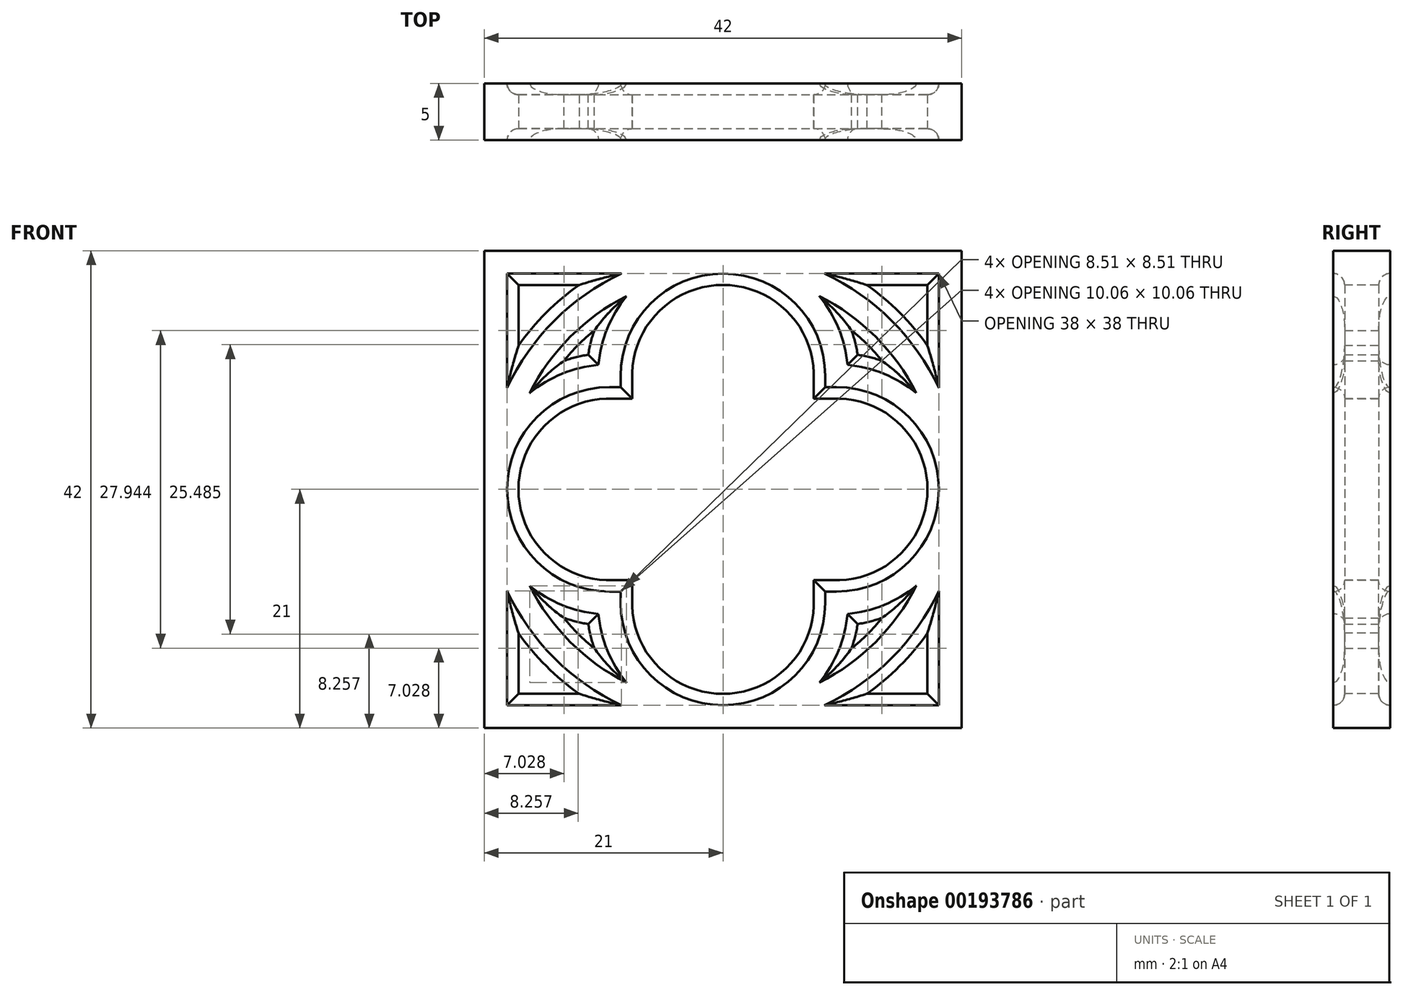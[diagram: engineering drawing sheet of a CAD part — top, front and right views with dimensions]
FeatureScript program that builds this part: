
annotation { "Feature Type Name" : "Feature", "Feature Type Description" : "" }
export const myFeature = defineFeature(function(context is Context, id is Id, definition is map)
    precondition{}
    {
        {
            var Q0;
            Q0=qCreatedBy(makeId("Right.planeOp"),FACE);
            var sketch = newSketch(context, id + "F0", { "sketchPlane" : qUnion([Q0])});
            skLineSegment(sketch, "E0", {"start": v(0, 0) * mm, "end": v(0, 20) * mm, "construction": true});
            skLineSegment(sketch, "E1.bottom", {"start": v(2.5, 21) * mm, "end": v(-2.5, 21) * mm});
            skLineSegment(sketch, "E1.top", {"start": v(2.5, 19) * mm, "end": v(-2.5, 19) * mm});
            skLineSegment(sketch, "E1.left", {"start": v(2.5, 21) * mm, "end": v(2.5, 19) * mm});
            skLineSegment(sketch, "E1.right", {"start": v(-2.5, 21) * mm, "end": v(-2.5, 19) * mm});
            skPoint(sketch, "E1.middle", {"position": v(0, 20) * mm});
            skLineSegment(sketch, "E2.bottom", {"start": v(-1.5, 22) * mm, "end": v(1.5, 22) * mm});
            skLineSegment(sketch, "E2.top", {"start": v(-1.5, 18) * mm, "end": v(1.5, 18) * mm});
            skLineSegment(sketch, "E2.left", {"start": v(-1.5, 22) * mm, "end": v(-1.5, 18) * mm});
            skLineSegment(sketch, "E2.right", {"start": v(1.5, 22) * mm, "end": v(1.5, 18) * mm});
            skArc(sketch, "E3", {"start": v(-2.5, 21) * mm, "mid": v(-1.8, 21.3) * mm, "end": v(-1.5, 22) * mm});
            skArc(sketch, "E4", {"start": v(-1.5, 18) * mm, "mid": v(-1.8, 18.7) * mm, "end": v(-2.5, 19) * mm});
            skArc(sketch, "E5", {"start": v(1.5, 22) * mm, "mid": v(1.8, 21.3) * mm, "end": v(2.5, 21) * mm});
            skArc(sketch, "E6", {"start": v(2.5, 19) * mm, "mid": v(1.8, 18.7) * mm, "end": v(1.5, 18) * mm});
            skLineSegment(sketch, "E7", {"start": v(0, 0) * mm, "end": v(-9.88, 0) * mm, "construction": true});
            skLineSegment(sketch, "E8", {"start": v(-2.5, 20) * mm, "end": v(2.5, 20) * mm});
            skSolve(sketch);
        }
        {
            var Q0;
            Q0=qCreatedBy(makeId("Front.planeOp"),FACE);
            var sketch = newSketch(context, id + "F1", { "sketchPlane" : qUnion([Q0])});
            skCircle(sketch, "E9", {"center": v(0, 0) * mm, "radius": 20 * mm});
            skLineSegment(sketch, "E10", {"start": v(0, 0) * mm, "end": v(20, 0) * mm, "construction": true});
            skLineSegment(sketch, "E11", {"start": v(0, 0) * mm, "end": v(-20, 0) * mm, "construction": true});
            skLineSegment(sketch, "E12", {"start": v(0, 0) * mm, "end": v(0, -20) * mm, "construction": true});
            skLineSegment(sketch, "E13", {"start": v(0, -20) * mm, "end": v(20, -20) * mm});
            skLineSegment(sketch, "E14", {"start": v(20, -20) * mm, "end": v(20, 0) * mm});
            skLineSegment(sketch, "E15", {"start": v(0, 0) * mm, "end": v(0, 20) * mm, "construction": true});
            skLineSegment(sketch, "E16", {"start": v(0, 20) * mm, "end": v(20, 20) * mm});
            skLineSegment(sketch, "E17", {"start": v(20, 20) * mm, "end": v(20, 0) * mm});
            skLineSegment(sketch, "E18", {"start": v(0, 20) * mm, "end": v(-20, 20) * mm});
            skLineSegment(sketch, "E19", {"start": v(-20, 20) * mm, "end": v(-20, 0) * mm});
            skLineSegment(sketch, "E20", {"start": v(0, -20) * mm, "end": v(-20, -20) * mm});
            skLineSegment(sketch, "E21", {"start": v(-20, -20) * mm, "end": v(-20, 0) * mm});
            skCircle(sketch, "E22", {"center": v(-10, 0) * mm, "radius": 10 * mm, "construction": true});
            skCircle(sketch, "E23", {"center": v(0, 10) * mm, "radius": 10 * mm, "construction": true});
            skCircle(sketch, "E24", {"center": v(10, 0) * mm, "radius": 10 * mm, "construction": true});
            skCircle(sketch, "E25", {"center": v(0, -10) * mm, "radius": 10 * mm, "construction": true});
            skArc(sketch, "E26", {"start": v(0, 20) * mm, "mid": v(-7.07, 17.07) * mm, "end": v(-10, 10) * mm});
            skArc(sketch, "E27", {"start": v(-10, 10) * mm, "mid": v(-17.07, 7.07) * mm, "end": v(-20, 0) * mm});
            skArc(sketch, "E28", {"start": v(-20, 0) * mm, "mid": v(-17.07, -7.07) * mm, "end": v(-10, -10) * mm});
            skArc(sketch, "E29", {"start": v(0, 20) * mm, "mid": v(7.07, 17.07) * mm, "end": v(10, 10) * mm});
            skArc(sketch, "E30", {"start": v(10, 10) * mm, "mid": v(17.07, 7.07) * mm, "end": v(20, 0) * mm});
            skArc(sketch, "E31", {"start": v(20, 0) * mm, "mid": v(17.07, -7.07) * mm, "end": v(10, -10) * mm});
            skArc(sketch, "E32", {"start": v(0, -20) * mm, "mid": v(7.07, -17.07) * mm, "end": v(10, -10) * mm});
            skArc(sketch, "E33", {"start": v(0, -20) * mm, "mid": v(-7.07, -17.07) * mm, "end": v(-10, -10) * mm});
            skLineSegment(sketch, "E34", {"start": v(0, 20) * mm, "end": v(0, 25) * mm, "construction": true});
            skLineSegment(sketch, "E35", {"start": v(0, 25) * mm, "end": v(25, 25) * mm});
            skLineSegment(sketch, "E36", {"start": v(25, 25) * mm, "end": v(25, -25) * mm});
            skLineSegment(sketch, "E37", {"start": v(25, -25) * mm, "end": v(-25, -25) * mm});
            skLineSegment(sketch, "E38", {"start": v(-25, -25) * mm, "end": v(-25, 25) * mm});
            skLineSegment(sketch, "E39", {"start": v(-25, 25) * mm, "end": v(0, 25) * mm});
            skPoint(sketch, "E40.0", {"position": v(0, 21) * mm});
            skLineSegment(sketch, "E41", {"start": v(0, 21) * mm, "end": v(21, 21) * mm});
            skLineSegment(sketch, "E42", {"start": v(21, 21) * mm, "end": v(21, -21) * mm});
            skLineSegment(sketch, "E43", {"start": v(21, -21) * mm, "end": v(-21, -21) * mm});
            skLineSegment(sketch, "E44", {"start": v(-21, -21) * mm, "end": v(-21, 21) * mm});
            skLineSegment(sketch, "E45", {"start": v(-21, 21) * mm, "end": v(0, 21) * mm});
            skSolve(sketch);
        }
        {
            var Q0;
            {var subQ0=sQuery(id+"F0.wireOp",EDGE,"E5");Q0=makeQuery(id+"F0.imprint","IMPRINT",FACE,{"disambiguationData":[TD([[makeQuery(id+"F0.imprint","IMPRINT",EDGE,{"derivedFrom":subQ0}),-1.0]])]});}
            var Q1;
            {var subQ1=sQuery(id+"F0.wireOp",EDGE,"E1.bottom");var subQ3=sQuery(id+"F0.wireOp",EDGE,"E2.right");var subQ4=makeQuery(id+"F0.imprint","INTERSECT",VERTEX,{"derivedFrom":[subQ1,subQ3]});Q1=makeQuery(id+"F0.imprint","IMPRINT",FACE,{"disambiguationData":[TD([[makeQuery(id+"F0.imprint","IMPRINT",EDGE,{"disambiguationData":[TD([[subQ4,-1.0]])],"derivedFrom":subQ3}),1.0]])]});}
            var Q2;
            {var subQ0=sQuery(id+"F0.wireOp",EDGE,"E2.right");var subQ1=sQuery(id+"F0.wireOp",EDGE,"E1.bottom");var subQ2=makeQuery(id+"F0.imprint","INTERSECT",VERTEX,{"derivedFrom":[subQ1,subQ0]});Q2=makeQuery(id+"F0.imprint","IMPRINT",FACE,{"disambiguationData":[TD([[makeQuery(id+"F0.imprint","IMPRINT",EDGE,{"disambiguationData":[TD([[subQ2,-1.0]])],"derivedFrom":subQ1}),1.0]])]});}
            var Q3;
            {var subQ5=sQuery(id+"F0.wireOp",EDGE,"E2.bottom");Q3=makeQuery(id+"F0.imprint","IMPRINT",FACE,{"disambiguationData":[TD([[makeQuery(id+"F0.imprint","IMPRINT",EDGE,{"derivedFrom":subQ5}),-1.0]])]});}
            var Q4;
            {var subQ0=sQuery(id+"F0.wireOp",EDGE,"E3");Q4=makeQuery(id+"F0.imprint","IMPRINT",FACE,{"disambiguationData":[TD([[makeQuery(id+"F0.imprint","IMPRINT",EDGE,{"derivedFrom":subQ0}),-1.0]])]});}
            var Q5;
            {var subQ1=sQuery(id+"F0.wireOp",EDGE,"E1.bottom");var subQ3=sQuery(id+"F0.wireOp",EDGE,"E2.left");var subQ4=makeQuery(id+"F0.imprint","INTERSECT",VERTEX,{"derivedFrom":[subQ1,subQ3]});Q5=makeQuery(id+"F0.imprint","IMPRINT",FACE,{"disambiguationData":[TD([[makeQuery(id+"F0.imprint","IMPRINT",EDGE,{"disambiguationData":[TD([[subQ4,-1.0]])],"derivedFrom":subQ3}),-1.0]])]});}
            var Q6;
            {var subQ1=sQuery(id+"F0.wireOp",EDGE,"E1.top");var subQ3=sQuery(id+"F0.wireOp",EDGE,"E2.left");var subQ4=makeQuery(id+"F0.imprint","INTERSECT",VERTEX,{"derivedFrom":[subQ1,subQ3]});Q6=makeQuery(id+"F0.imprint","IMPRINT",FACE,{"disambiguationData":[TD([[makeQuery(id+"F0.imprint","IMPRINT",EDGE,{"disambiguationData":[TD([[subQ4,1.0]])],"derivedFrom":subQ3}),-1.0]])]});}
            var Q7;
            {var subQ0=sQuery(id+"F0.wireOp",EDGE,"E2.right");var subQ1=sQuery(id+"F0.wireOp",EDGE,"E1.top");var subQ2=makeQuery(id+"F0.imprint","INTERSECT",VERTEX,{"derivedFrom":[subQ1,subQ0]});Q7=makeQuery(id+"F0.imprint","IMPRINT",FACE,{"disambiguationData":[TD([[makeQuery(id+"F0.imprint","IMPRINT",EDGE,{"disambiguationData":[TD([[subQ2,-1.0]])],"derivedFrom":subQ1}),-1.0]])]});}
            var Q8;
            {var subQ5=sQuery(id+"F0.wireOp",EDGE,"E2.top");Q8=makeQuery(id+"F0.imprint","IMPRINT",FACE,{"disambiguationData":[TD([[makeQuery(id+"F0.imprint","IMPRINT",EDGE,{"derivedFrom":subQ5}),1.0]])]});}
            var Q9;
            {var subQ0=sQuery(id+"F0.wireOp",EDGE,"E4");Q9=makeQuery(id+"F0.imprint","IMPRINT",FACE,{"disambiguationData":[TD([[makeQuery(id+"F0.imprint","IMPRINT",EDGE,{"derivedFrom":subQ0}),-1.0]])]});}
            var Q10;
            {var subQ1=sQuery(id+"F0.wireOp",EDGE,"E1.top");var subQ3=sQuery(id+"F0.wireOp",EDGE,"E2.right");var subQ4=makeQuery(id+"F0.imprint","INTERSECT",VERTEX,{"derivedFrom":[subQ1,subQ3]});Q10=makeQuery(id+"F0.imprint","IMPRINT",FACE,{"disambiguationData":[TD([[makeQuery(id+"F0.imprint","IMPRINT",EDGE,{"disambiguationData":[TD([[subQ4,1.0]])],"derivedFrom":subQ3}),1.0]])]});}
            var Q11;
            {var subQ0=sQuery(id+"F0.wireOp",EDGE,"E6");Q11=makeQuery(id+"F0.imprint","IMPRINT",FACE,{"disambiguationData":[TD([[makeQuery(id+"F0.imprint","IMPRINT",EDGE,{"derivedFrom":subQ0}),-1.0]])]});}
            var Q12;
            Q12=sQuery(id+"F1.wireOp",EDGE,"E9");
            sweep(context, id + "F2", {"profiles" : qUnion([Q0, Q1, Q2, Q3, Q4, Q5, Q6, Q7, Q8, Q9, Q10, Q11]), "path" : qUnion([Q12])});
        }
        {
            var Q0;
            {var subQ1=sQuery(id+"F0.wireOp",EDGE,"E1.bottom");var subQ3=sQuery(id+"F0.wireOp",EDGE,"E2.left");var subQ4=makeQuery(id+"F0.imprint","INTERSECT",VERTEX,{"derivedFrom":[subQ1,subQ3]});Q0=makeQuery(id+"F0.imprint","IMPRINT",FACE,{"disambiguationData":[TD([[makeQuery(id+"F0.imprint","IMPRINT",EDGE,{"disambiguationData":[TD([[subQ4,-1.0]])],"derivedFrom":subQ3}),-1.0]])]});}
            var Q1;
            {var subQ1=sQuery(id+"F0.wireOp",EDGE,"E1.top");var subQ3=sQuery(id+"F0.wireOp",EDGE,"E2.left");var subQ4=makeQuery(id+"F0.imprint","INTERSECT",VERTEX,{"derivedFrom":[subQ1,subQ3]});Q1=makeQuery(id+"F0.imprint","IMPRINT",FACE,{"disambiguationData":[TD([[makeQuery(id+"F0.imprint","IMPRINT",EDGE,{"disambiguationData":[TD([[subQ4,1.0]])],"derivedFrom":subQ3}),-1.0]])]});}
            var Q2;
            {var subQ0=sQuery(id+"F0.wireOp",EDGE,"E2.right");var subQ1=sQuery(id+"F0.wireOp",EDGE,"E1.bottom");var subQ2=makeQuery(id+"F0.imprint","INTERSECT",VERTEX,{"derivedFrom":[subQ1,subQ0]});Q2=makeQuery(id+"F0.imprint","IMPRINT",FACE,{"disambiguationData":[TD([[makeQuery(id+"F0.imprint","IMPRINT",EDGE,{"disambiguationData":[TD([[subQ2,-1.0]])],"derivedFrom":subQ1}),1.0]])]});}
            var Q3;
            {var subQ0=sQuery(id+"F0.wireOp",EDGE,"E2.right");var subQ1=sQuery(id+"F0.wireOp",EDGE,"E1.top");var subQ2=makeQuery(id+"F0.imprint","INTERSECT",VERTEX,{"derivedFrom":[subQ1,subQ0]});Q3=makeQuery(id+"F0.imprint","IMPRINT",FACE,{"disambiguationData":[TD([[makeQuery(id+"F0.imprint","IMPRINT",EDGE,{"disambiguationData":[TD([[subQ2,-1.0]])],"derivedFrom":subQ1}),-1.0]])]});}
            var Q4;
            {var subQ0=sQuery(id+"F0.wireOp",EDGE,"E4");Q4=makeQuery(id+"F0.imprint","IMPRINT",FACE,{"disambiguationData":[TD([[makeQuery(id+"F0.imprint","IMPRINT",EDGE,{"derivedFrom":subQ0}),-1.0]])]});}
            var Q5;
            {var subQ5=sQuery(id+"F0.wireOp",EDGE,"E2.top");Q5=makeQuery(id+"F0.imprint","IMPRINT",FACE,{"disambiguationData":[TD([[makeQuery(id+"F0.imprint","IMPRINT",EDGE,{"derivedFrom":subQ5}),1.0]])]});}
            var Q6;
            {var subQ1=sQuery(id+"F0.wireOp",EDGE,"E1.bottom");var subQ3=sQuery(id+"F0.wireOp",EDGE,"E2.right");var subQ4=makeQuery(id+"F0.imprint","INTERSECT",VERTEX,{"derivedFrom":[subQ1,subQ3]});Q6=makeQuery(id+"F0.imprint","IMPRINT",FACE,{"disambiguationData":[TD([[makeQuery(id+"F0.imprint","IMPRINT",EDGE,{"disambiguationData":[TD([[subQ4,-1.0]])],"derivedFrom":subQ3}),1.0]])]});}
            var Q7;
            {var subQ1=sQuery(id+"F0.wireOp",EDGE,"E1.top");var subQ3=sQuery(id+"F0.wireOp",EDGE,"E2.right");var subQ4=makeQuery(id+"F0.imprint","INTERSECT",VERTEX,{"derivedFrom":[subQ1,subQ3]});Q7=makeQuery(id+"F0.imprint","IMPRINT",FACE,{"disambiguationData":[TD([[makeQuery(id+"F0.imprint","IMPRINT",EDGE,{"disambiguationData":[TD([[subQ4,1.0]])],"derivedFrom":subQ3}),1.0]])]});}
            var Q8;
            {var subQ0=sQuery(id+"F0.wireOp",EDGE,"E6");Q8=makeQuery(id+"F0.imprint","IMPRINT",FACE,{"disambiguationData":[TD([[makeQuery(id+"F0.imprint","IMPRINT",EDGE,{"derivedFrom":subQ0}),-1.0]])]});}
            var Q9;
            Q9=sQuery(id+"F1.wireOp",EDGE,"E16");
            var Q10;
            Q10=sQuery(id+"F1.wireOp",EDGE,"E17");
            var Q11;
            Q11=sQuery(id+"F1.wireOp",EDGE,"E14");
            var Q12;
            Q12=sQuery(id+"F1.wireOp",EDGE,"E13");
            var Q13;
            Q13=sQuery(id+"F1.wireOp",EDGE,"E20");
            var Q14;
            Q14=sQuery(id+"F1.wireOp",EDGE,"E21");
            var Q15;
            Q15=sQuery(id+"F1.wireOp",EDGE,"E19");
            var Q16;
            Q16=sQuery(id+"F1.wireOp",EDGE,"E18");
            sweep(context, id + "F3", {"operationType" : NewBodyOperationType.ADD, "profiles" : qUnion([Q0, Q1, Q2, Q3, Q4, Q5, Q6, Q7, Q8]), "path" : qUnion([Q9, Q10, Q11, Q12, Q13, Q14, Q15, Q16])});
        }
        {
            var Q0;
            {var subQ1=sQuery(id+"F0.wireOp",EDGE,"E1.bottom");var subQ3=sQuery(id+"F0.wireOp",EDGE,"E2.right");var subQ4=makeQuery(id+"F0.imprint","INTERSECT",VERTEX,{"derivedFrom":[subQ1,subQ3]});Q0=makeQuery(id+"F0.imprint","IMPRINT",FACE,{"disambiguationData":[TD([[makeQuery(id+"F0.imprint","IMPRINT",EDGE,{"disambiguationData":[TD([[subQ4,-1.0]])],"derivedFrom":subQ3}),1.0]])]});}
            var Q1;
            {var subQ1=sQuery(id+"F0.wireOp",EDGE,"E1.top");var subQ3=sQuery(id+"F0.wireOp",EDGE,"E2.right");var subQ4=makeQuery(id+"F0.imprint","INTERSECT",VERTEX,{"derivedFrom":[subQ1,subQ3]});Q1=makeQuery(id+"F0.imprint","IMPRINT",FACE,{"disambiguationData":[TD([[makeQuery(id+"F0.imprint","IMPRINT",EDGE,{"disambiguationData":[TD([[subQ4,1.0]])],"derivedFrom":subQ3}),1.0]])]});}
            var Q2;
            {var subQ0=sQuery(id+"F0.wireOp",EDGE,"E2.right");var subQ1=sQuery(id+"F0.wireOp",EDGE,"E1.bottom");var subQ2=makeQuery(id+"F0.imprint","INTERSECT",VERTEX,{"derivedFrom":[subQ1,subQ0]});Q2=makeQuery(id+"F0.imprint","IMPRINT",FACE,{"disambiguationData":[TD([[makeQuery(id+"F0.imprint","IMPRINT",EDGE,{"disambiguationData":[TD([[subQ2,-1.0]])],"derivedFrom":subQ1}),1.0]])]});}
            var Q3;
            {var subQ0=sQuery(id+"F0.wireOp",EDGE,"E2.right");var subQ1=sQuery(id+"F0.wireOp",EDGE,"E1.top");var subQ2=makeQuery(id+"F0.imprint","INTERSECT",VERTEX,{"derivedFrom":[subQ1,subQ0]});Q3=makeQuery(id+"F0.imprint","IMPRINT",FACE,{"disambiguationData":[TD([[makeQuery(id+"F0.imprint","IMPRINT",EDGE,{"disambiguationData":[TD([[subQ2,-1.0]])],"derivedFrom":subQ1}),-1.0]])]});}
            var Q4;
            {var subQ5=sQuery(id+"F0.wireOp",EDGE,"E2.top");Q4=makeQuery(id+"F0.imprint","IMPRINT",FACE,{"disambiguationData":[TD([[makeQuery(id+"F0.imprint","IMPRINT",EDGE,{"derivedFrom":subQ5}),1.0]])]});}
            var Q5;
            {var subQ0=sQuery(id+"F0.wireOp",EDGE,"E6");Q5=makeQuery(id+"F0.imprint","IMPRINT",FACE,{"disambiguationData":[TD([[makeQuery(id+"F0.imprint","IMPRINT",EDGE,{"derivedFrom":subQ0}),-1.0]])]});}
            var Q6;
            {var subQ5=sQuery(id+"F0.wireOp",EDGE,"E2.bottom");Q6=makeQuery(id+"F0.imprint","IMPRINT",FACE,{"disambiguationData":[TD([[makeQuery(id+"F0.imprint","IMPRINT",EDGE,{"derivedFrom":subQ5}),-1.0]])]});}
            var Q7;
            {var subQ0=sQuery(id+"F0.wireOp",EDGE,"E5");Q7=makeQuery(id+"F0.imprint","IMPRINT",FACE,{"disambiguationData":[TD([[makeQuery(id+"F0.imprint","IMPRINT",EDGE,{"derivedFrom":subQ0}),-1.0]])]});}
            var Q8;
            {var subQ0=sQuery(id+"F0.wireOp",EDGE,"E3");Q8=makeQuery(id+"F0.imprint","IMPRINT",FACE,{"disambiguationData":[TD([[makeQuery(id+"F0.imprint","IMPRINT",EDGE,{"derivedFrom":subQ0}),-1.0]])]});}
            var Q9;
            {var subQ1=sQuery(id+"F0.wireOp",EDGE,"E1.bottom");var subQ3=sQuery(id+"F0.wireOp",EDGE,"E2.left");var subQ4=makeQuery(id+"F0.imprint","INTERSECT",VERTEX,{"derivedFrom":[subQ1,subQ3]});Q9=makeQuery(id+"F0.imprint","IMPRINT",FACE,{"disambiguationData":[TD([[makeQuery(id+"F0.imprint","IMPRINT",EDGE,{"disambiguationData":[TD([[subQ4,-1.0]])],"derivedFrom":subQ3}),-1.0]])]});}
            var Q10;
            {var subQ1=sQuery(id+"F0.wireOp",EDGE,"E1.top");var subQ3=sQuery(id+"F0.wireOp",EDGE,"E2.left");var subQ4=makeQuery(id+"F0.imprint","INTERSECT",VERTEX,{"derivedFrom":[subQ1,subQ3]});Q10=makeQuery(id+"F0.imprint","IMPRINT",FACE,{"disambiguationData":[TD([[makeQuery(id+"F0.imprint","IMPRINT",EDGE,{"disambiguationData":[TD([[subQ4,1.0]])],"derivedFrom":subQ3}),-1.0]])]});}
            var Q11;
            {var subQ0=sQuery(id+"F0.wireOp",EDGE,"E4");Q11=makeQuery(id+"F0.imprint","IMPRINT",FACE,{"disambiguationData":[TD([[makeQuery(id+"F0.imprint","IMPRINT",EDGE,{"derivedFrom":subQ0}),-1.0]])]});}
            var Q12;
            Q12=sQuery(id+"F1.wireOp",EDGE,"E29");
            var Q13;
            Q13=sQuery(id+"F1.wireOp",EDGE,"E30");
            var Q14;
            Q14=sQuery(id+"F1.wireOp",EDGE,"E31");
            var Q15;
            Q15=sQuery(id+"F1.wireOp",EDGE,"E32");
            var Q16;
            Q16=sQuery(id+"F1.wireOp",EDGE,"E33");
            var Q17;
            Q17=sQuery(id+"F1.wireOp",EDGE,"E28");
            var Q18;
            Q18=sQuery(id+"F1.wireOp",EDGE,"E27");
            var Q19;
            Q19=sQuery(id+"F1.wireOp",EDGE,"E26");
            sweep(context, id + "F4", {"operationType" : NewBodyOperationType.ADD, "profiles" : qUnion([Q0, Q1, Q2, Q3, Q4, Q5, Q6, Q7, Q8, Q9, Q10, Q11]), "path" : qUnion([Q12, Q13, Q14, Q15, Q16, Q17, Q18, Q19])});
        }
        {
            var Q0;
            Q0=makeQuery(id+"F1.imprint","IMPRINT",FACE,{"disambiguationData":[TD([[makeQuery(id+"F1.imprint","IMPRINT",EDGE,{"derivedFrom":sQuery(id+"F1.wireOp",EDGE,"E35")}),-1.0]])]});
            extrude(context, id + "F5", {"entities" : qUnion([Q0]), "operationType" : NewBodyOperationType.REMOVE, "endBound" : BoundingType.SYMMETRIC, "oppositeDirection" : true, "depth" : 10 * mm});
        }
    });
